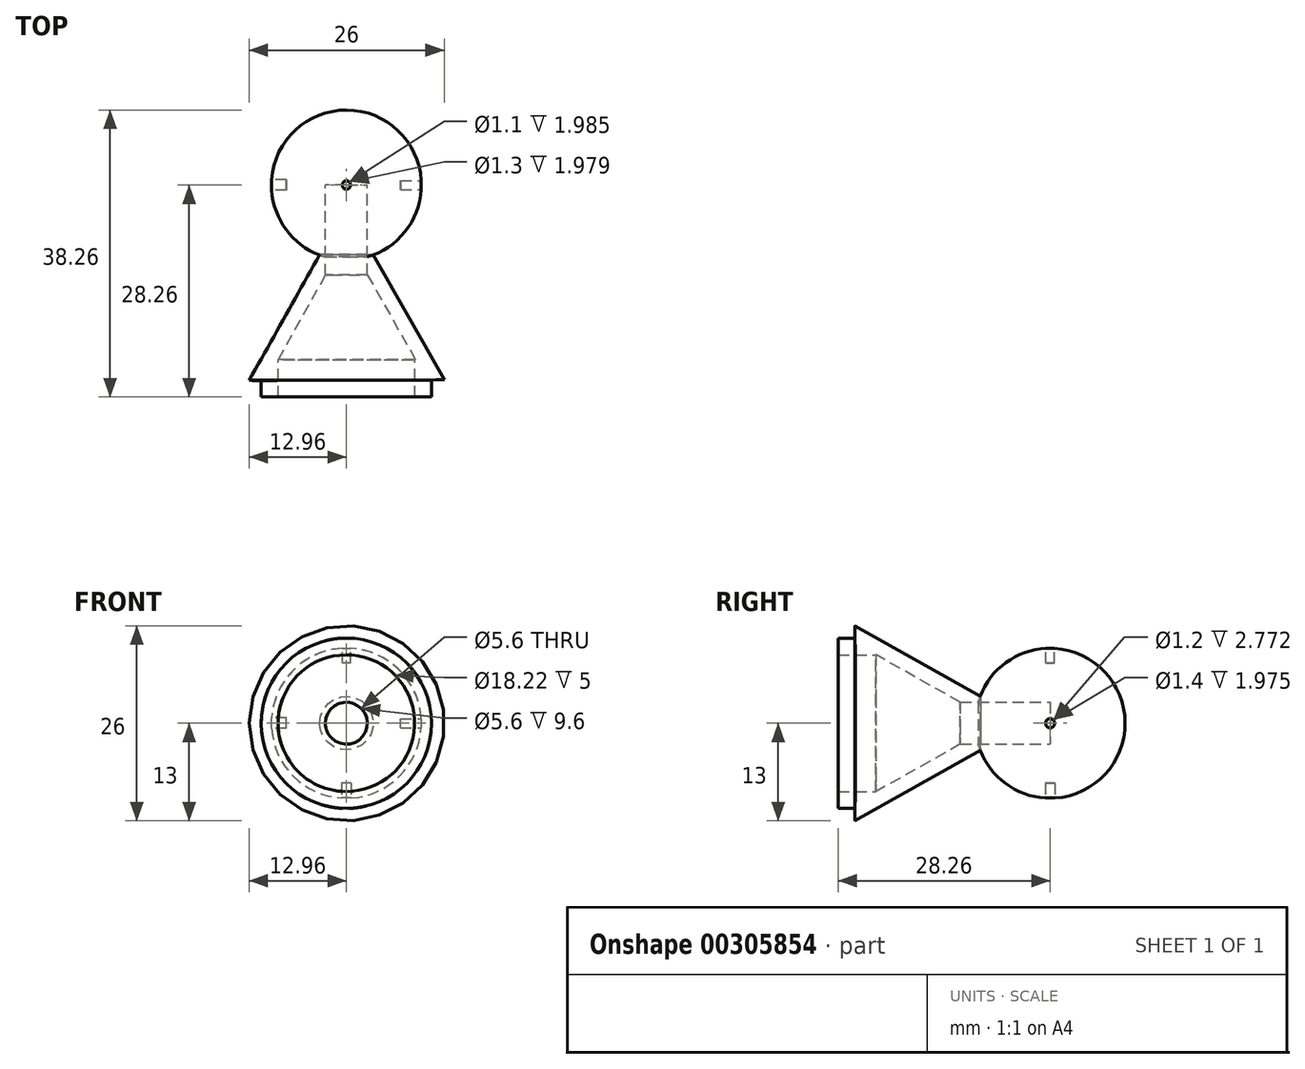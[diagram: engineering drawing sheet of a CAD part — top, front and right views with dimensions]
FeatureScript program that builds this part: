
annotation { "Feature Type Name" : "Feature", "Feature Type Description" : "" }
export const myFeature = defineFeature(function(context is Context, id is Id, definition is map)
    precondition{}
    {
        {
            var Q0;
            Q0=qCreatedBy(makeId("Front.planeOp"),FACE);
            var sketch = newSketch(context, id + "F0", { "sketchPlane" : qUnion([Q0])});
            skPoint(sketch, "E0.endSnap0", {"position": v(0, -12.5) * mm});
            skArc(sketch, "E1", {"start": v(-10, 0) * mm, "mid": v(0, -10) * mm, "end": v(10, 0) * mm});
            skLineSegment(sketch, "E2", {"start": v(-10, 0) * mm, "end": v(10, 0) * mm});
            skSolve(sketch);
        }
        {
            var Q0;
            Q0=makeQuery(id+"F0.imprint","IMPRINT",FACE,{"disambiguationData":[TD([[makeQuery(id+"F0.imprint","IMPRINT",EDGE,{"derivedFrom":sQuery(id+"F0.wireOp",EDGE,"E1")}),1.0]])]});
            var Q1;
            Q1=sQuery(id+"F0.wireOp",EDGE,"E2");
            revolve(context, id + "F1", {"entities" : qUnion([Q0]), "axis" : qUnion([Q1]), "revolveType" : RevolveType.FULL});
        }
        {
            var Q0;
            Q0=qCreatedBy(makeId("Right.planeOp"),FACE);
            cPlane(context, id + "F2", {"entities" : qUnion([Q0]), "cplaneType" : CPlaneType.OFFSET, "offset" : 10 * mm, "width" : 150 * mm, "height" : 150 * mm});
        }
        {
            var Q0;
            Q0=qCreatedBy(makeId("Top.planeOp"),FACE);
            cPlane(context, id + "F3", {"entities" : qUnion([Q0]), "cplaneType" : CPlaneType.OFFSET, "offset" : 10 * mm, "width" : 150 * mm, "height" : 150 * mm});
        }
        {
            var Q0;
            Q0=qCreatedBy(makeId("Top.planeOp"),FACE);
            cPlane(context, id + "F4", {"entities" : qUnion([Q0]), "cplaneType" : CPlaneType.OFFSET, "offset" : 10 * mm, "oppositeDirection" : true, "width" : 150 * mm, "height" : 150 * mm});
        }
        {
            var Q0;
            Q0=qCreatedBy(makeId("Right.planeOp"),FACE);
            cPlane(context, id + "F5", {"entities" : qUnion([Q0]), "cplaneType" : CPlaneType.OFFSET, "offset" : 10 * mm, "oppositeDirection" : true, "width" : 150 * mm, "height" : 150 * mm});
        }
        {
            var Q0;
            Q0=qCreatedBy(id+"F2.planeOp",FACE);
            var sketch = newSketch(context, id + "F6", { "sketchPlane" : qUnion([Q0])});
            skCircle(sketch, "E3", {"center": v(0, 0) * mm, "radius": 0.6 * mm});
            skSolve(sketch);
        }
        {
            var Q0;
            Q0=qCreatedBy(id+"F3.planeOp",FACE);
            var sketch = newSketch(context, id + "F7", { "sketchPlane" : qUnion([Q0])});
            skCircle(sketch, "E4", {"center": v(0, 0) * mm, "radius": 0.55 * mm});
            skSolve(sketch);
        }
        {
            var Q0;
            Q0=qCreatedBy(id+"F4.planeOp",FACE);
            var sketch = newSketch(context, id + "F8", { "sketchPlane" : qUnion([Q0])});
            skCircle(sketch, "E5", {"center": v(0, 0) * mm, "radius": 0.65 * mm});
            skSolve(sketch);
        }
        {
            var Q0;
            Q0=qCreatedBy(id+"F5.planeOp",FACE);
            var sketch = newSketch(context, id + "F9", { "sketchPlane" : qUnion([Q0])});
            skCircle(sketch, "E6", {"center": v(0, 0) * mm, "radius": 0.7 * mm});
            skSolve(sketch);
        }
        {
            var Q0;
            Q0=qSketchRegion(id+"F6",true);
            extrude(context, id + "F10", {"entities" : qUnion([Q0]), "operationType" : NewBodyOperationType.REMOVE, "endBound" : BoundingType.SYMMETRIC, "oppositeDirection" : true, "depth" : 5.58 * mm});
        }
        {
            var Q0;
            Q0=qSketchRegion(id+"F7",true);
            extrude(context, id + "F11", {"entities" : qUnion([Q0]), "operationType" : NewBodyOperationType.REMOVE, "oppositeDirection" : true, "depth" : 2 * mm});
        }
        {
            var Q0;
            Q0=qSketchRegion(id+"F8",true);
            extrude(context, id + "F12", {"entities" : qUnion([Q0]), "operationType" : NewBodyOperationType.REMOVE, "depth" : 2 * mm});
        }
        {
            var Q0;
            Q0=qSketchRegion(id+"F9",true);
            extrude(context, id + "F13", {"entities" : qUnion([Q0]), "operationType" : NewBodyOperationType.REMOVE, "depth" : 2 * mm});
        }
        {
            var Q0;
            Q0=qCreatedBy(makeId("Front.planeOp"),FACE);
            cPlane(context, id + "F14", {"entities" : qUnion([Q0]), "cplaneType" : CPlaneType.OFFSET, "offset" : 23.1 * mm, "width" : 150 * mm, "height" : 150 * mm});
        }
        {
            var Q0;
            Q0=qCreatedBy(makeId("Top.planeOp"),FACE);
            var sketch = newSketch(context, id + "F15", { "sketchPlane" : qUnion([Q0])});
            skLineSegment(sketch, "E7", {"start": v(-3.57, -9.28) * mm, "end": v(-12.96, -26.05) * mm});
            skLineSegment(sketch, "E8.right", {"start": v(-3.57, -9.28) * mm, "end": v(-3.57, -9.28) * mm});
            skLineSegment(sketch, "E9", {"start": v(-12.96, -26.05) * mm, "end": v(0.04, -26.21) * mm});
            skLineSegment(sketch, "E10", {"start": v(0, -9.28) * mm, "end": v(0.04, -26.21) * mm});
            skLineSegment(sketch, "E11", {"start": v(-3.57, -9.28) * mm, "end": v(0, -9.28) * mm});
            skSolve(sketch);
        }
        {
            var Q0;
            Q0 = qSketchRegion(id + "F15", true);
            var Q1;
            Q1=sQuery(id+"F15.wireOp",EDGE,"E10");
            revolve(context, id + "F16", {"entities" : qUnion([Q0]), "axis" : qUnion([Q1]), "revolveType" : RevolveType.FULL});
        }
        {
            var Q0;
            Q0=makeQuery(id+"F16.opRevolve","SWEPT_FACE",FACE,{"disambiguationData":[OSD([sQuery(id+"F15.wireOp",EDGE,"E7")])]});
            var Q1;
            Q1=makeQuery(id+"F16.opRevolve","SWEPT_BODY",BODY,{"disambiguationData":[OSD([sQuery(id+"F15.wireOp",EDGE,"E7"),sQuery(id+"F15.wireOp",EDGE,"E9"),sQuery(id+"F15.wireOp",EDGE,"m10rvklH-Jax2-fBEv-3tPO-sINxGn2oZyp3"),sQuery(id+"F15.wireOp",EDGE,"E10")])]});
            shell(context, id + "F17", {"isHollow" : true, "entities" : qUnion([Q0]), "parts" : qUnion([Q1]), "thickness" : 2 * mm});
        }
        {
            var Q0;
            Q0=qCreatedBy(id+"F14.planeOp",FACE);
            cPlane(context, id + "F18", {"entities" : qUnion([Q0]), "cplaneType" : CPlaneType.OFFSET, "offset" : 2.91 * mm, "width" : 150 * mm, "height" : 150 * mm});
        }
        {
            var Q0;
            Q0=qCreatedBy(id+"F18.planeOp",FACE);
            var sketch = newSketch(context, id + "F19", { "sketchPlane" : qUnion([Q0])});
            skCircle(sketch, "E12", {"center": v(0, 0) * mm, "radius": 11.35 * mm});
            skSolve(sketch);
        }
        {
            var Q0;
            Q0 = qSketchRegion(id + "F19", true);
            extrude(context, id + "F20", {"entities" : qUnion([Q0]), "operationType" : NewBodyOperationType.REMOVE, "endBound" : BoundingType.SYMMETRIC, "oppositeDirection" : true, "depth" : 5.5 * mm});
        }
        {
            var Q0;
            Q0=qCreatedBy(makeId("Front.planeOp"),FACE);
            var sketch = newSketch(context, id + "F21", { "sketchPlane" : qUnion([Q0])});
            skCircle(sketch, "E13", {"center": v(0, 0) * mm, "radius": 2.8 * mm});
            skSolve(sketch);
        }
        {
            var Q0;
            Q0=qSketchRegion(id+"F21",true);
            var Q1;
            Q1=sQuery(id+"F21.wireOp",EDGE,"E13");
            extrude(context, id + "F22", {"entities" : qUnion([Q0]), "operationType" : NewBodyOperationType.REMOVE, "surfaceEntities" : qUnion([Q1]), "endBound" : BoundingType.THROUGH_ALL, "depth" : 50 * mm});
        }
        {
            var Q0;
            Q0=makeQuery(id+"F20.boolean.opBoolean","COPY",FACE,{"derivedFrom":makeQuery(id+"F20.opExtrude","CAP_FACE",FACE,{"disambiguationData":[OSD([sQuery(id+"F19.wireOp",EDGE,"E12")])],"isStart":false})});
            var sketch = newSketch(context, id + "F23", { "sketchPlane" : qUnion([Q0])});
            skCircle(sketch, "E14", {"center": v(0, 0) * mm, "radius": 11.35 * mm});
            skCircle(sketch, "E15", {"center": v(0, 0) * mm, "radius": 9.11 * mm});
            skSolve(sketch);
        }
        {
            var Q0;
            Q0 = qSketchRegion(id + "F23", true);
            extrude(context, id + "F24", {"entities" : qUnion([Q0]), "operationType" : NewBodyOperationType.ADD, "depth" : 5 * mm});
        }
    });
